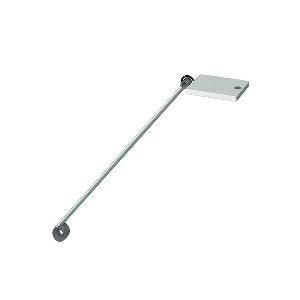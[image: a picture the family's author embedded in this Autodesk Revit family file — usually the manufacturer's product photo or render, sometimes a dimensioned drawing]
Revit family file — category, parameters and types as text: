
# Revit family: para_mi_-_mftl_108_r__930_00644003_584d
name_source: partatom
category: Lighting Fixtures
units: mm (PartAtom-declared; Revit-internal decimal feet)

## family parameters
Cut with Voids When Loaded = No
Host = Face
Light Source = No
Part Type = Normal
Room Calculation Point = No
Round Connector Dimension = Use Diameter
Shared = No

## types (1)
- PARA.MI - MFTL 108 R /930 (1 x LED, 580 lm, 3000K)
    Apparent Load = 7 VA
    Approval mark = CE
    CIE Flux Codes = 70 94 99 100 100
    Color Rendering = 90-100
    Color Temperature = 3000K
    Control Gear = Electronic ballast
    Default Elevation = 1800 mm
    Description = MFTL 108 R|Task luminaire|light source: LED|work equipment: Electronic plug-in transformer|connected load: 100-240 V, 50/60 Hz|Power consumption: approx. 7 W|luminous flux: 580 lm|luminous efficacy: 82 lm/W|Illuminance efficiency factor: 107 lx/W|colour temperature: Warm white, ca. 3000 K|color rendering index (CRI): >= 90|chromaticity tolerance:  3 SDCM|class of protection: II with plug-in power supply, III without plug-in power supply|technology: Continuously dimmable|luminaire body|material: Aluminium|surface: Painted|colour: Silver|lamp cover: Plastic, Clear|tubular sections|material: Tubular aluminium section|surface: Painted|colour: Silver metallic|weight (net): approx. 0.7 kg|mains lead: 3.00 m Mains plug BS 1363, CEE 7/XVI, NEMA 1-15P|Fastening: Adaptor (accessory), Table base (accessory), Table clamp (accessory), Tap16|glare control: Reflector|special features: Automatic switchoff adjustable, Push button in luminaire head, Behaviour at net recovery adjustable|Approval mark: C - ETL - US (F. CAN U. USA), VDE - ENEC SEP LIGHT & POWER SUPPLY UNIT|
    Height = 12 mm  [stored 0.0393701 ft]
    Lamp = 1 x LED
    Lamp Light Flux = 580 lm
    Lamp count = 1
    Length = 123 mm
    Luminous efficacy = 83 lm/W
    Manufacturer = Waldmann
    ModVariant = No
    Model = 00644003
    Mounting Place = Table
    Mounting Type = Surface mounted
    Number of Poles = 1
    OnlyDefault = Yes
    Power Factor = 1
    Product Name = PARA.MI - MFTL 108 R /930
    Product group = Task luminaire (office)
    ProductGroupID = 21
    Protection Class = Protection class II
    Protection Degree = IP 40
    RLX_Detail_Level = 1
    RLX_Emergency_Light_Flux = 0 lm
    RLX_Emergency_Type = 0
    RLX_Emergency_Type_DB = No
    RlxData = <blob elided: 53041 chars, md5=124ba26c>
    Socket = socket
    Standby Power = 0 W
    System Light Flux = 580 lm
    System Power = 7 W
    Type Comments = Product without accessories
    Type Image = 113149000-00644014.jpg
    URL = http://relux.com
    VarID = ---
    Voltage = 230 V
    Voltage Range = 220-240 V
    Weight = 0.00 kg
    Width = 0 mm  [stored 0 ft]

note: [stored X ft] marks values corroborated as IEEE doubles in the binary element streams (Revit-internal decimal feet)

## geometry (parser evidence)
native form markers: Blend x4, Sweep x14
no freeform markers — native parametric forms only
